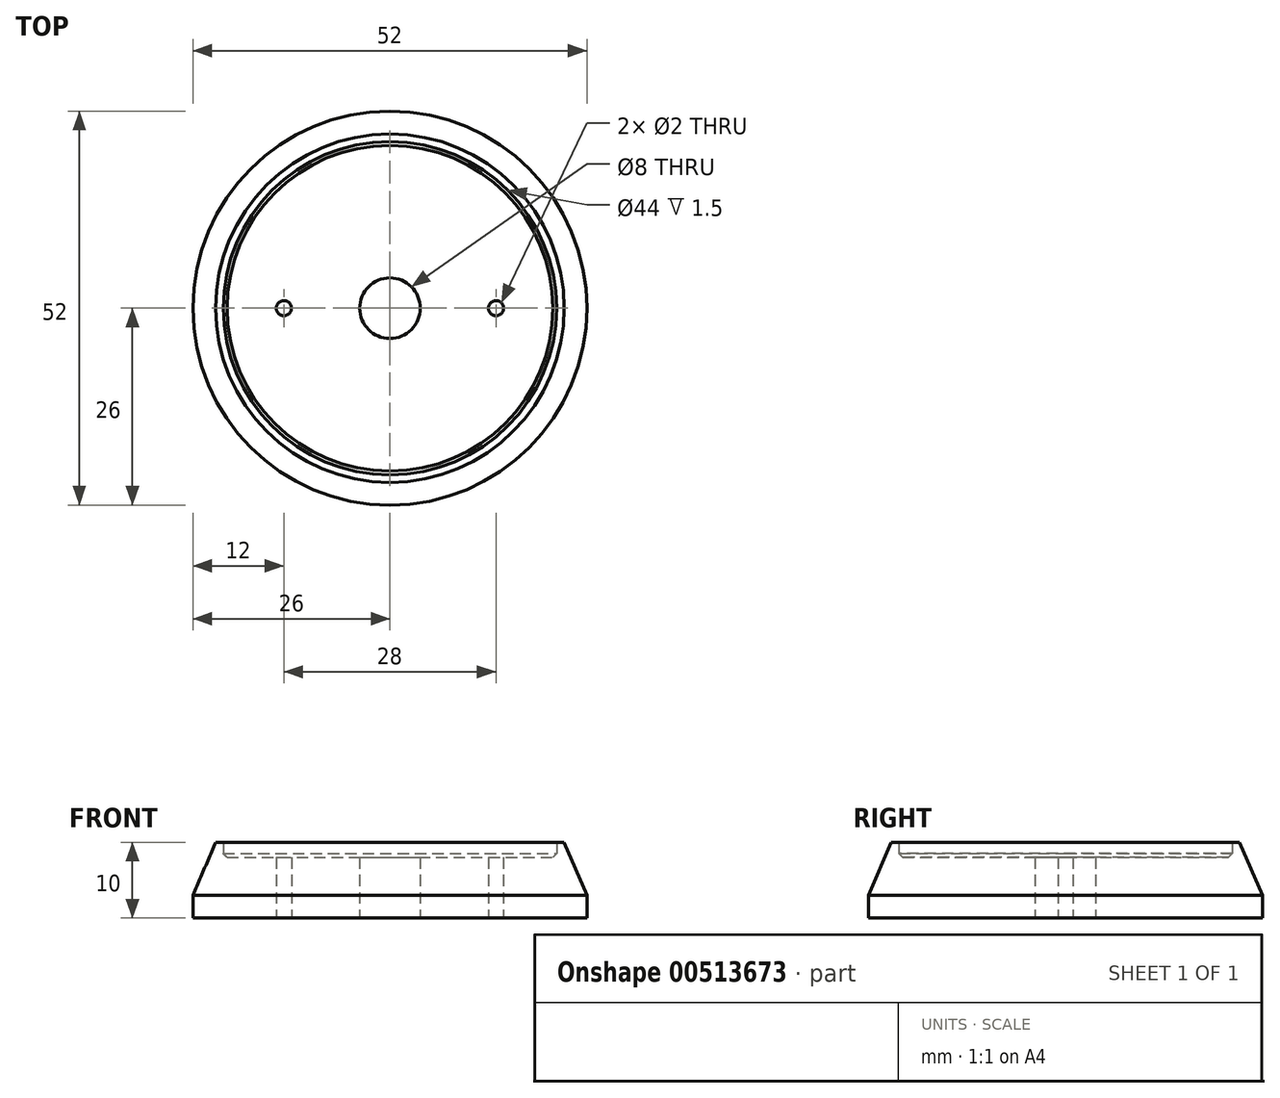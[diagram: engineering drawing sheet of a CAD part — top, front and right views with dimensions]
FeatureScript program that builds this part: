
annotation { "Feature Type Name" : "Feature", "Feature Type Description" : "" }
export const myFeature = defineFeature(function(context is Context, id is Id, definition is map)
    precondition{}
    {
        {
            var Q0;
            Q0=qCreatedBy(makeId("Front.planeOp"),FACE);
            var sketch = newSketch(context, id + "F0", { "sketchPlane" : qUnion([Q0])});
            skLineSegment(sketch, "E0", {"start": v(0, 21.4) * mm, "end": v(-26, 21.4) * mm});
            skLineSegment(sketch, "E1", {"start": v(0, 21.4) * mm, "end": v(0, 29.4) * mm});
            skLineSegment(sketch, "E2", {"start": v(0, 29.4) * mm, "end": v(-21.5, 29.4) * mm});
            skLineSegment(sketch, "E3", {"start": v(-4, 29.4) * mm, "end": v(-4, 21.4) * mm});
            skLineSegment(sketch, "E4", {"start": v(-26, 21.4) * mm, "end": v(-26, 24.4) * mm});
            skLineSegment(sketch, "E5", {"start": v(-26, 24.4) * mm, "end": v(-23, 31.4) * mm});
            skLineSegment(sketch, "E6", {"start": v(-23, 31.4) * mm, "end": v(-22, 31.4) * mm});
            skLineSegment(sketch, "E7", {"start": v(-22, 31.4) * mm, "end": v(-22, 29.9) * mm});
            skLineSegment(sketch, "E8", {"start": v(-22, 29.9) * mm, "end": v(-21.5, 29.4) * mm});
            skSolve(sketch);
        }
        {
            var Q0;
            {var subQ0=sQuery(id+"F0.wireOp",EDGE,"E3");Q0=makeQuery(id+"F0.imprint","IMPRINT",FACE,{"disambiguationData":[TD([[makeQuery(id+"F0.imprint","IMPRINT",EDGE,{"derivedFrom":subQ0}),-1.0]])]});}
            var Q1;
            Q1=sQuery(id+"F0.wireOp",EDGE,"E1");
            revolve(context, id + "F1", {"entities" : qUnion([Q0]), "axis" : qUnion([Q1]), "revolveType" : RevolveType.FULL});
        }
        {
            var Q0;
            Q0=makeQuery(id+"F1.opRevolve","SWEPT_FACE",FACE,{"disambiguationData":[OSD([sQuery(id+"F0.wireOp",EDGE,"E0")])]});
            var sketch = newSketch(context, id + "F2", { "sketchPlane" : qUnion([Q0])});
            skPoint(sketch, "E9", {"position": v(-14, 0) * mm});
            skPoint(sketch, "E10.1.0", {"position": v(14, 0) * mm});
            skPoint(sketch, "E10.center", {"position": v(0, 0) * mm});
            skSolve(sketch);
        }
        {
            var Q0;
            Q0=sQuery(id+"F2.wireOp",VERTEX,"E9");
            var Q1;
            Q1=sQuery(id+"F2.wireOp",VERTEX,"E10.1.0");
            var Q2;
            Q2=makeQuery(id+"F1.opRevolve","SWEPT_BODY",BODY,{"disambiguationData":[OSD([sQuery(id+"F0.wireOp",EDGE,"E0"),sQuery(id+"F0.wireOp",EDGE,"E2"),sQuery(id+"F0.wireOp",EDGE,"I1IZs9et-yzp2-pkoH-Uqyj-Zst5VyObDKE9"),sQuery(id+"F0.wireOp",EDGE,"TEGZxwhD-VCsi-AP2g-Tj0f-wSHnz4qmJ26e"),sQuery(id+"F0.wireOp",EDGE,"TgjRPXJ9-tEQl-qVCL-aCPt-cUJG5a0YcU9j"),sQuery(id+"F0.wireOp",EDGE,"E3")])]});
            hole(context, id + "F3", {"style" : HoleStyle.SIMPLE, "endStyle" : HoleEndStyle.THROUGH, "holeDiameter" : 2 * mm, "isTappedThrough" : true, "tappedDepth" : 12 * mm, "tapClearance" : 3, "locations" : qUnion([Q0, Q1]), "scope" : qUnion([Q2])});
        }
    });
